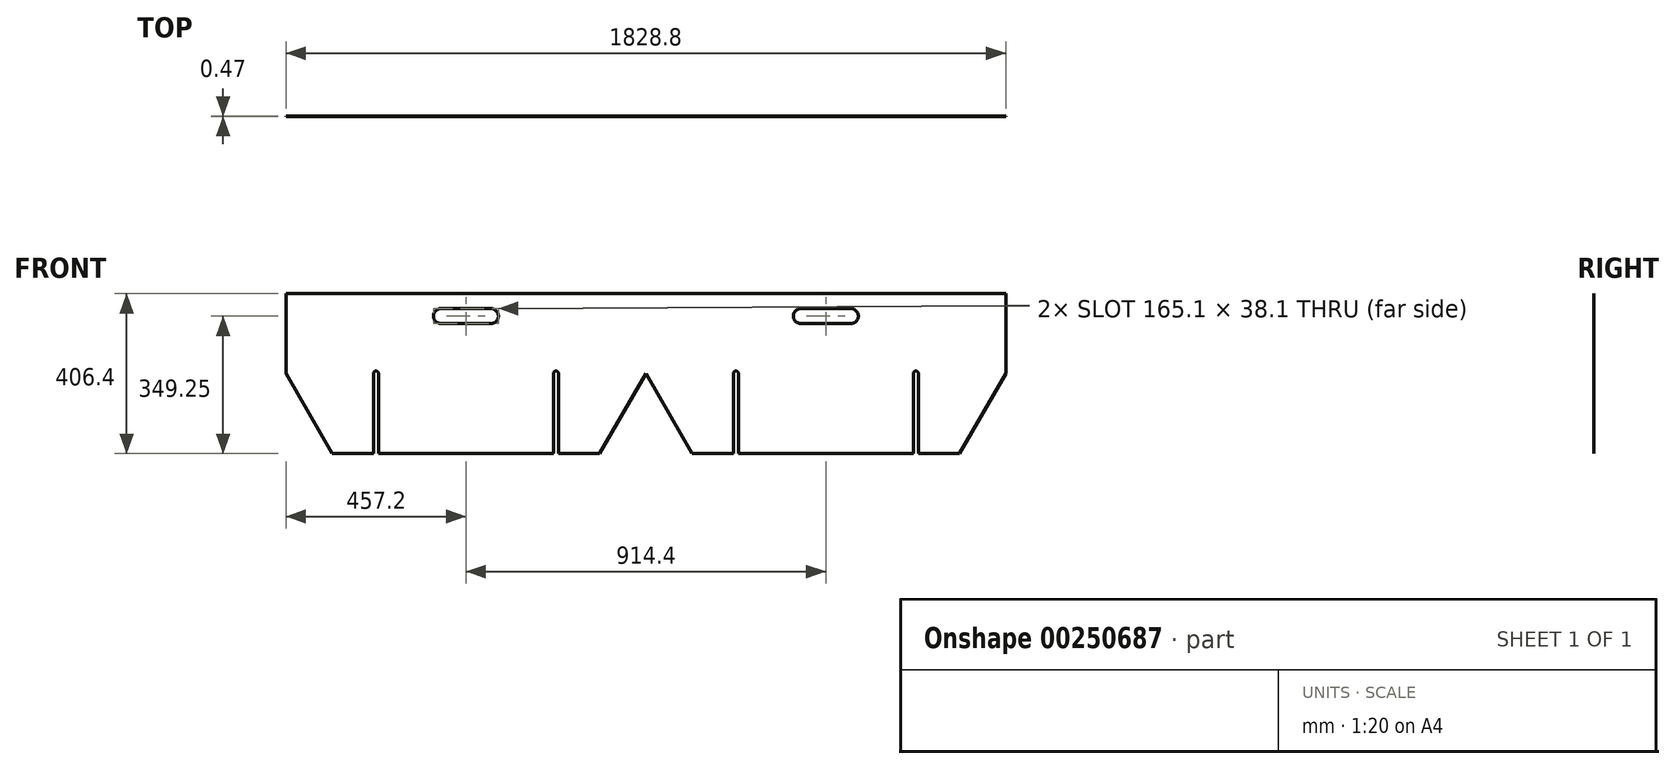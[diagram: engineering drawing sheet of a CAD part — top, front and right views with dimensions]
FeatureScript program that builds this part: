
annotation { "Feature Type Name" : "Feature", "Feature Type Description" : "" }
export const myFeature = defineFeature(function(context is Context, id is Id, definition is map)
    precondition{}
    {
        {
            assignVariable(context, id + "F0", {"name" : "Thickness", "anyValue" : 15 / 32});
        }
        {
            var Q0;
            Q0=qCreatedBy(makeId("Front.planeOp"),FACE);
            var sketch = newSketch(context, id + "F1", { "sketchPlane" : qUnion([Q0])});
            skLineSegment(sketch, "E0.bottom", {"start": v(0, 406.4) * mm, "end": v(914.4, 406.4) * mm});
            skLineSegment(sketch, "E0.top", {"start": v(117.32, 0) * mm, "end": v(222.25, 0) * mm});
            skLineSegment(sketch, "E0.left", {"start": v(0, 406.4) * mm, "end": v(0, 203.2) * mm});
            skLineSegment(sketch, "E0.right", {"start": v(914.4, 406.4) * mm, "end": v(914.4, 0) * mm, "construction": true});
            skLineSegment(sketch, "E1", {"start": v(0, 203.2) * mm, "end": v(117.32, 0) * mm});
            skLineSegment(sketch, "E2.MirrorCS", {"start": v(1828.8, 406.4) * mm, "end": v(914.4, 406.4) * mm});
            skLineSegment(sketch, "E3.MirrorCS", {"start": v(1828.8, 406.4) * mm, "end": v(1828.8, 203.2) * mm});
            skLineSegment(sketch, "E4.MirrorCS", {"start": v(1828.8, 203.2) * mm, "end": v(1711.48, 0) * mm});
            skLineSegment(sketch, "E5.MirrorCS", {"start": v(1711.48, 0) * mm, "end": v(1606.55, 0) * mm});
            skPoint(sketch, "E6", {"position": v(228.6, 0) * mm});
            skPoint(sketch, "E7", {"position": v(685.8, 0) * mm});
            skLineSegment(sketch, "E8", {"start": v(685.8, 0) * mm, "end": v(685.8, 203.2) * mm, "construction": true});
            skLineSegment(sketch, "E9", {"start": v(228.6, 0) * mm, "end": v(228.6, 203.2) * mm, "construction": true});
            skArc(sketch, "E10", {"start": v(234.95, 203.2) * mm, "mid": v(228.6, 209.55) * mm, "end": v(222.25, 203.2) * mm});
            skPoint(sketch, "E11.orphan", {"position": v(0, 0) * mm});
            skArc(sketch, "E12", {"start": v(692.15, 203.2) * mm, "mid": v(685.8, 209.55) * mm, "end": v(679.45, 203.2) * mm});
            skLineSegment(sketch, "E13", {"start": v(222.25, 203.2) * mm, "end": v(222.25, 0) * mm});
            skLineSegment(sketch, "E14", {"start": v(234.95, 203.2) * mm, "end": v(234.95, 0) * mm});
            skLineSegment(sketch, "E15", {"start": v(679.45, 203.2) * mm, "end": v(679.45, 0) * mm});
            skLineSegment(sketch, "E16", {"start": v(692.15, 203.2) * mm, "end": v(692.15, 0) * mm});
            skLineSegment(sketch, "E17.trimOffspring", {"start": v(692.15, 0) * mm, "end": v(797.08, 0) * mm});
            skLineSegment(sketch, "E18.trimOffspring", {"start": v(234.95, 0) * mm, "end": v(679.45, 0) * mm});
            skArc(sketch, "E19.MirrorCS", {"start": v(1136.65, 203.2) * mm, "mid": v(1143, 209.55) * mm, "end": v(1149.35, 203.2) * mm});
            skLineSegment(sketch, "E20.MirrorCS", {"start": v(1136.65, 203.2) * mm, "end": v(1136.65, 0) * mm});
            skLineSegment(sketch, "E21.MirrorCS", {"start": v(1149.35, 203.2) * mm, "end": v(1149.35, 0) * mm});
            skLineSegment(sketch, "E22.MirrorCS", {"start": v(1593.85, 203.2) * mm, "end": v(1593.85, 0) * mm});
            skArc(sketch, "E23.MirrorCS", {"start": v(1593.85, 203.2) * mm, "mid": v(1600.2, 209.55) * mm, "end": v(1606.55, 203.2) * mm});
            skLineSegment(sketch, "E24.MirrorCS", {"start": v(1606.55, 203.2) * mm, "end": v(1606.55, 0) * mm});
            skLineSegment(sketch, "E25.trimOffspring", {"start": v(1136.65, 0) * mm, "end": v(1031.72, 0) * mm});
            skLineSegment(sketch, "E26.trimOffspring", {"start": v(1593.85, 0) * mm, "end": v(1149.35, 0) * mm});
            skPoint(sketch, "E27.orphan", {"position": v(1828.8, 0) * mm});
            skLineSegment(sketch, "E28", {"start": v(457.2, 406.4) * mm, "end": v(457.2, 368.3) * mm, "construction": true});
            skLineSegment(sketch, "E29", {"start": v(457.2, 368.3) * mm, "end": v(393.7, 368.3) * mm});
            skLineSegment(sketch, "E30", {"start": v(457.2, 368.3) * mm, "end": v(457.2, 330.2) * mm, "construction": true});
            skLineSegment(sketch, "E31", {"start": v(457.2, 330.2) * mm, "end": v(393.7, 330.2) * mm});
            skArc(sketch, "E32", {"start": v(393.7, 368.3) * mm, "mid": v(374.65, 349.25) * mm, "end": v(393.7, 330.2) * mm});
            skLineSegment(sketch, "E33.MirrorCS", {"start": v(457.2, 368.3) * mm, "end": v(520.7, 368.3) * mm});
            skArc(sketch, "E34.MirrorCS", {"start": v(520.7, 368.3) * mm, "mid": v(539.75, 349.25) * mm, "end": v(520.7, 330.2) * mm});
            skLineSegment(sketch, "E35.MirrorCS", {"start": v(457.2, 330.2) * mm, "end": v(520.7, 330.2) * mm});
            skLineSegment(sketch, "E36.MirrorCS", {"start": v(1371.6, 368.3) * mm, "end": v(1308.1, 368.3) * mm});
            skArc(sketch, "E37.MirrorCS", {"start": v(1308.1, 368.3) * mm, "mid": v(1289.05, 349.25) * mm, "end": v(1308.1, 330.2) * mm});
            skLineSegment(sketch, "E38.MirrorCS", {"start": v(1371.6, 330.2) * mm, "end": v(1308.1, 330.2) * mm});
            skLineSegment(sketch, "E39.MirrorCS", {"start": v(1371.6, 330.2) * mm, "end": v(1435.1, 330.2) * mm});
            skArc(sketch, "E40.MirrorCS", {"start": v(1435.1, 368.3) * mm, "mid": v(1454.15, 349.25) * mm, "end": v(1435.1, 330.2) * mm});
            skLineSegment(sketch, "E41.MirrorCS", {"start": v(1371.6, 368.3) * mm, "end": v(1435.1, 368.3) * mm});
            skLineSegment(sketch, "E42", {"start": v(914.4, 203.2) * mm, "end": v(797.08, 0) * mm});
            skLineSegment(sketch, "E43.MirrorCS", {"start": v(914.4, 203.2) * mm, "end": v(1031.72, 0) * mm});
            skPoint(sketch, "E44.orphan", {"position": v(914.4, 0) * mm});
            skSolve(sketch);
        }
        {
            var Q0;
            Q0=makeQuery(id+"F1.imprint","IMPRINT",FACE,{"disambiguationData":[TD([[makeQuery(id+"F1.imprint","IMPRINT",EDGE,{"derivedFrom":sQuery(id+"F1.wireOp",EDGE,"E0.bottom")}),-1.0]])]});
            extrude(context, id + "F2", {"entities" : qUnion([Q0]), "depth" : (getVariable(context, 'Thickness')) * mm});
        }
    });
